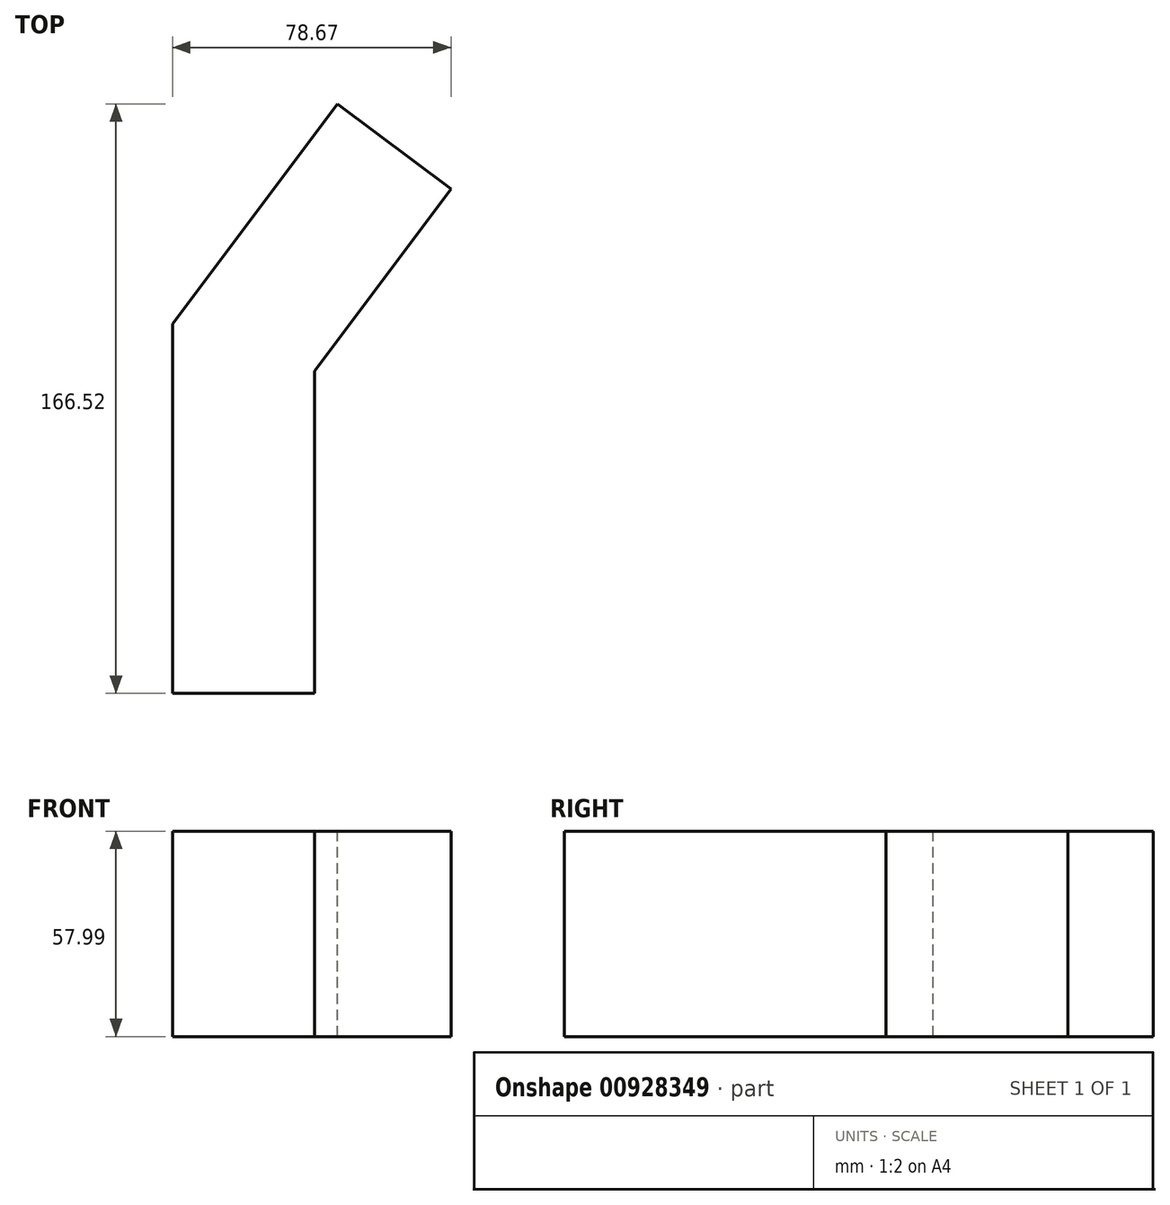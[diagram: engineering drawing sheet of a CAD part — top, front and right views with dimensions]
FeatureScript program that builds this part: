
annotation { "Feature Type Name" : "Feature", "Feature Type Description" : "" }
export const myFeature = defineFeature(function(context is Context, id is Id, definition is map)
    precondition{}
    {
        {
            var Q0;
            Q0=qCreatedBy(makeId("Front.planeOp"),FACE);
            var sketch = newSketch(context, id + "F0", { "sketchPlane" : qUnion([Q0])});
            skLineSegment(sketch, "E0.bottom", {"start": v(0, 0) * mm, "end": v(-40.08, 0) * mm});
            skLineSegment(sketch, "E0.top", {"start": v(0, 57.99) * mm, "end": v(-40.08, 57.99) * mm});
            skLineSegment(sketch, "E0.left", {"start": v(0, 0) * mm, "end": v(0, 57.99) * mm});
            skLineSegment(sketch, "E0.right", {"start": v(-40.08, 0) * mm, "end": v(-40.08, 57.99) * mm});
            skSolve(sketch);
        }
        {
            var Q0;
            Q0=qCreatedBy(makeId("Top.planeOp"),FACE);
            var sketch = newSketch(context, id + "F1", { "sketchPlane" : qUnion([Q0])});
            skLineSegment(sketch, "E1", {"start": v(-40.08, 0) * mm, "end": v(-40.08, 104.36) * mm});
            skLineSegment(sketch, "E2", {"start": v(-40.08, 104.36) * mm, "end": v(6.53, 166.52) * mm});
            skSolve(sketch);
        }
        {
            var Q0;
            Q0=makeQuery(id+"F0.imprint","IMPRINT",FACE,{"disambiguationData":[TD([[makeQuery(id+"F0.imprint","IMPRINT",EDGE,{"derivedFrom":sQuery(id+"F0.wireOp",EDGE,"E0.bottom")}),-1.0]])]});
            var Q1;
            Q1=sQuery(id+"F1.wireOp",EDGE,"E1");
            var Q2;
            Q2=sQuery(id+"F1.wireOp",EDGE,"E2");
            sweep(context, id + "F2", {"profiles" : qUnion([Q0]), "path" : qUnion([Q1, Q2])});
        }
    });
